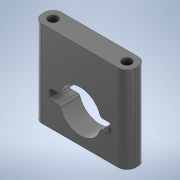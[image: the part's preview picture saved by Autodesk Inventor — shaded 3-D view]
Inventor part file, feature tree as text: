
AUTODESK INVENTOR PART (.ipt)
format: ipt  version: 2020 (Build 240168000, 168)  size: 188,928 bytes
history: native  units: mm
features: projected_geometry x7, sketch x4, extrude x3, fillet x2, other x1
ambient origin geometry x8: Origin, YZ Plane, XZ Plane, XY Plane, X Axis, Y Axis, Z Axis, Center Point
bodies: Body1 (feature_tree)
feature tree (17):
  other  "Твердое тело1"
  sketch  "Эскиз1"
  extrude  "Выдавливание1"  Depth=30.0mm
  fillet  "Сопряжение1"  Radius=3.8mm
  extrude  "Выдавливание2"  Depth=38.0mm
  extrude  "Выдавливание3"  Depth=8.0mm
  fillet  "Сопряжение2"  Radius=35.0mm
  sketch  "Эскиз2"
  sketch  "Эскиз3"
  projected_geometry  "Спроецированная петля1"
  projected_geometry  "Спроецированная петля2"
  projected_geometry  "Спроецированная петля3"
  projected_geometry  "Спроецированная петля4"
  projected_geometry  "Спроецированная петля5"
  projected_geometry  "Спроецированная петля6"
  sketch  "Эскиз4"
  projected_geometry  "Спроецированная петля7"
